# Revit family: 00-5697-05-DC
name_source: partatom
category: Luminarias
revit_build: Autodesk Revit 2017 (Build: 20160225_1515(x64)
units: mm (PartAtom-declared; Revit-internal decimal feet)

## family parameters
Anfitrión = Cara
Compartido = Sí
Corte con vacíos al cargar = No
Cota de conector redondo = Diámetro de uso
Número OmniClass = 23.80.70.00
Origen de luz = No
Punto de cálculo de habitación = No
Tipo de pieza = Normal
Título OmniClass = Lighting

## types (1)
- 00-5697-05-DC
    Acabado = Negro, Cemento
    CRI = 80
    Carga aparente = 0 VA
    Catálogo = Decorative
    CodigoGubimclass = 50.60.50.20
    CodigoOmniclass = 21-04 50 40
    CodigoUniclass2015 = EF_70_80
    CodigoUniformat2010 = D5040
    DescripcionGubimclass = Iluminación interior
    DescripcionOmniclass = Lighting
    DescripcionUniclass2015 = Lighting
    DescripcionUniformat2010 = Lighting
    EAN13 = 8435381494513
    Eficiencia energética = LED A++
    Elevación por defecto = 1000 mm  [stored 3.28084 ft]
    Etiqueta V/f = 100-240V/50-60Hz
    Fabricante = LEDS C4
    Familia = Eclipse Tubular
    FechaVersion = Julio 2020
    Ficha = http://files.leds-c4.com
    Fotometría = http://files.leds-c4.com
    Fuente de luz = 1xLED 7 615.00 lm
    IMC = http://files.leds-c4.com
    IP = IP20
    IfcExportAs = IfcLightFixture
IfcLightFixture
    IfcExportType = NOTDEFINED
    Imagen web = http://files.leds-c4.com
    LDT = http://files.leds-c4.com
    Lumenes reales (lm) = 118
    Material = Acero, Cemento
    Peso neto (KG) = 0.92
    Pluma comercial = http://files.leds-c4.com
    Producto descatalogado = Catalogado ES
    Rayo de luz = FLOOD
    Referencia = 00-5697-05-DC
    Temperatura color led (K) = Blanco cálido - 2700K
    Tender text (Castellano) = LEDS C4
Eclipse Tubular
00-5697-05-DCV2

Colgante de uso interior para iluminar hacia abajo. 
Material estructura: Acero, Cemento. Acabado estructura: Negro, Cemento. Garantía: 5 Años.

Peso neto del producto (Kg): 0.920
Anchura o diámetro del producto (mm): Ø110
Altura del producto (mm): Max 1800

Clase 2. IP: IP20. LED. Longitud máxima de la bombilla que admite la luminaria: 1825.000. Diámetro máximo de la bombilla que admite la luminaria: 100.000. Nº de portalámparas o Leds: 1. Marca del LED: CREE. Marca del Driver: EAGLERISE. Potencia máxima de la fuente de luz: 7W. Temperatura de color: Blanco cálido - 2700K. Índice de reproducción cromática: 80. Steps Mac Adam: 2. Diámetro máximo de la bombilla que admite la luminaria: 50.000h L80B20. UGR:  17.3. Riesgo fotobiológico: RG1. Flujo real (lm): 118. Flujo nominal (lm): 615. Lm/W reales: 14. Rango de voltaje/frecuencia: 100-240. Voltaje: 9. Equipo incluido: Si, electrónico. Potencia total: 8.6. Factor de potencia: 0.55.
    Tender text (English) = LEDS C4
Eclipse Tubular
00-5697-05-DCV2

Pendant for indoor use. 

For downlighting. Structure material: Steel, cement. Structure finish: Black, Cement. Warranty: 5 Years.

Product net weight (Kg): 0.920
Product width or diameter (mm): Ø110
Product height (mm): Max 1800

Class 2. IP: IP20. LED. Maximum length of luminaire bulb: 1825.000. Maximum diameter of luminaire bulb: 100.000. No. of lampholders or LEDs: 1. LED brand: CREE. Driver brand: EAGLERISE. Maximum power of light source: 7W. Colour temperature: LED warm-white 2700K. Colour rendering index: 80. MacAdam Steps: 2. Maximum diameter of luminaire bulb: 50.000h L80B20. UGR:  17.3. Photobiological risk: RG1. Real flux (lm): 118. Nominal flux (lm): 615. Lm/Real W: 14. Voltage and frequency range: 100-240. Voltage: 9. Gear included: Yes, electronic. Total power: 8.6. Power factor: 0.55.
    Tipo = Colgante
    Vatios (W) = 8.6
    Versión = v1

note: [stored X ft] marks values corroborated as IEEE doubles in the binary element streams (Revit-internal decimal feet)
